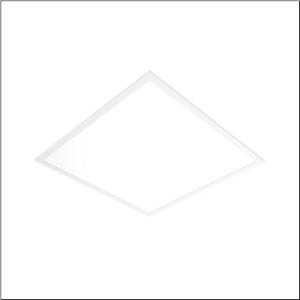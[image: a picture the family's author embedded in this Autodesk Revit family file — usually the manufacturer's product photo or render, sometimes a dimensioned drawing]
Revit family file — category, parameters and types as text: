
# Revit family: apollon_r__41_51mh11w72n43_7a0e
name_source: partatom
category: Lighting Fixtures
units: mm (PartAtom-declared; Revit-internal decimal feet)

## family parameters
Cut with Voids When Loaded = No
Host = Face
Light Source = No
Part Type = Normal
Room Calculation Point = No
Round Connector Dimension = Use Diameter
Shared = No

## types (1)
- --- (1 x LED, 3600 lm, 28.5 W, 6500K)
    Apparent Load = 29 VA
    CIE Flux Codes = 61 87 97 100 100
    Color Rendering = 80
    Color Temperature = 6500K
    Default Elevation = 1800 mm
    Description = Apollon® 41, office luminaire, primary optical cover: prismatic diffuser, of PS, light emission: direct distribution, primary light characteristic: symmetric, installation type: lay-in mounting, LED, rated luminous flux: 3.700lm, luminous efficacy: 130lm/W, light colour: 840/865, colour temperature: 4000/6500K, with terminal, 3-pole, mains connection: 220..240V, AC, 50/60Hz, housing, of aluminium section, traffic white (RAL 9016), module: M625, length: 620mm, width: 620mm, height: 28mm, housing upper side, of sheet steel, protection rating (complete): IP20, protection rating (lamp compartment, on room side): IP40, insulation class (complete): insulation class II (safety insulation), certification: CE, ENEC, permissible operating ambient temperature: -25..+40°C, packaging unit: 1 piece
    Height = 0 mm  [stored 0 ft]
    Lamp = 1 x LED
    Lamp Light Flux = 3600 lm
    Lamp Power = 28.5 W
    Lamp count = 1
    Length = 620 mm
    Luminous efficacy = 126 lm/W
    Manufacturer = Siteco
    ModVariant = No
    Model = 51MH11W72N43
    Mounting Place = Ceiling
    Mounting Type = Recessed
    Number of Poles = 1
    OnlyDefault = Yes
    Power Factor = 1
    Product Name = Apollon® 41
    Product group = office luminaire | ceiling recessed
    ProductGroupID = 401
    Protection Class = Protection class II
    Protection Degree = IP 20
    RLX_Detail_Level = 1
    RLX_Emergency_Light_Flux = 0 lm
    RLX_Emergency_Type = 0
    RLX_Emergency_Type_DB = No
    RlxData = <blob elided: 12405 chars, md5=30303969>
    Socket = socket
    Standby Power = 0 W
    System Light Flux = 3600 lm
    System Power = 29 W
    Type Comments = individual setting
    Type Image = l_1291024.jpg
    URL = http://relux.com
    VarID = @adj_008959
    Voltage = 0 V
    Weight = 0.00 kg
    Width = 620 mm

note: [stored X ft] marks values corroborated as IEEE doubles in the binary element streams (Revit-internal decimal feet)

## geometry (parser evidence)
native form markers: Sweep x11
no freeform markers — native parametric forms only
